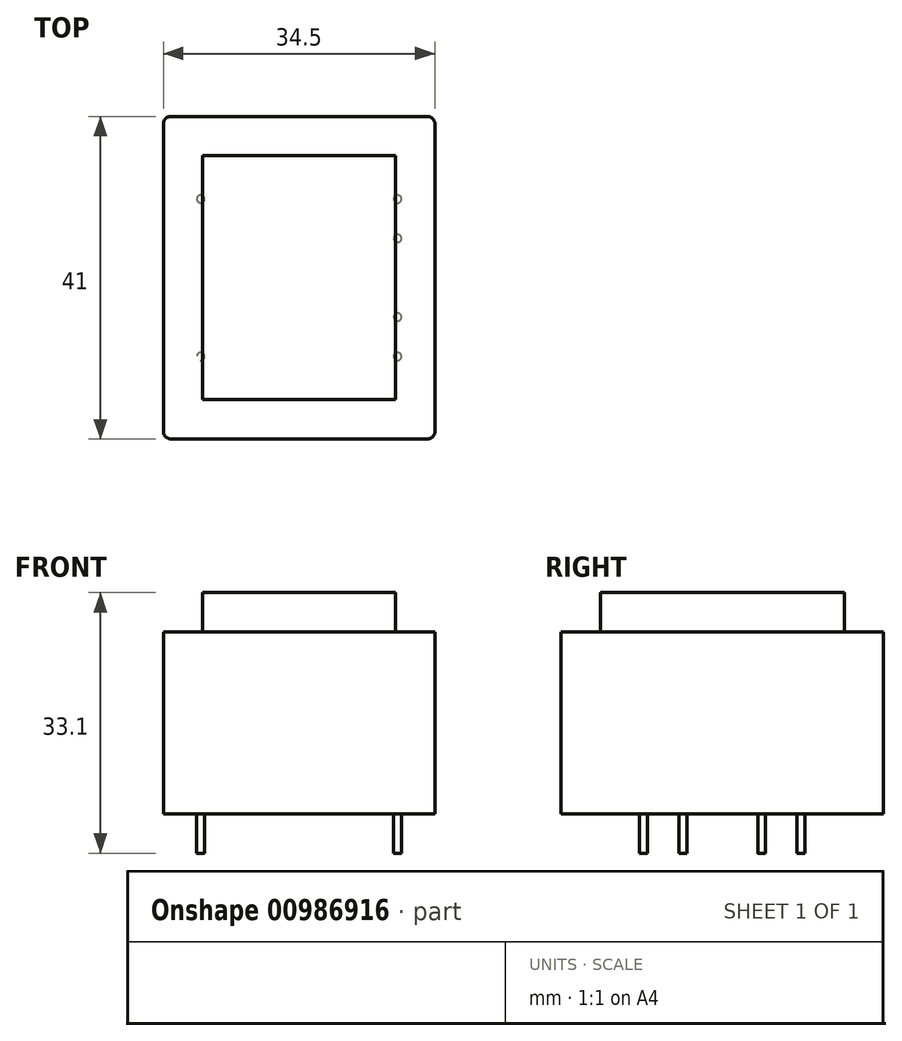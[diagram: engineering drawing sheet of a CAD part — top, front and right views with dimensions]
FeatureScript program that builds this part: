
annotation { "Feature Type Name" : "Feature", "Feature Type Description" : "" }
export const myFeature = defineFeature(function(context is Context, id is Id, definition is map)
    precondition{}
    {
        {
            var Q0;
            Q0=qCreatedBy(makeId("Top.planeOp"),FACE);
            var sketch = newSketch(context, id + "F0", { "sketchPlane" : qUnion([Q0])});
            skLineSegment(sketch, "E0.bottom", {"start": v(17.25, 20.5) * mm, "end": v(-17.25, 20.5) * mm});
            skLineSegment(sketch, "E0.top", {"start": v(17.25, -20.5) * mm, "end": v(-17.25, -20.5) * mm});
            skLineSegment(sketch, "E0.left", {"start": v(17.25, 20.5) * mm, "end": v(17.25, -20.5) * mm});
            skLineSegment(sketch, "E0.right", {"start": v(-17.25, 20.5) * mm, "end": v(-17.25, -20.5) * mm});
            skPoint(sketch, "E0.middle", {"position": v(0, 0) * mm});
            skSolve(sketch);
        }
        {
            var Q0;
            Q0=makeQuery(id+"F0.imprint","IMPRINT",FACE,{"disambiguationData":[TD([[makeQuery(id+"F0.imprint","IMPRINT",EDGE,{"derivedFrom":sQuery(id+"F0.wireOp",EDGE,"E0.bottom")}),1.0]])]});
            extrude(context, id + "F1", {"entities" : qUnion([Q0]), "depth" : 28.1 * mm, "offsetDistance" : 25 * mm});
        }
        {
            var Q0;
            Q0=makeQuery(id+"F1.opExtrude","CAP_FACE",FACE,{"disambiguationData":[OSD([sQuery(id+"F0.wireOp",EDGE,"E0.bottom"),sQuery(id+"F0.wireOp",EDGE,"E0.top"),sQuery(id+"F0.wireOp",EDGE,"E0.left"),sQuery(id+"F0.wireOp",EDGE,"E0.right")])],"isStart":true});
            var sketch = newSketch(context, id + "F2", { "sketchPlane" : qUnion([Q0])});
            skLineSegment(sketch, "E1.bottom", {"start": v(12.5, 10) * mm, "end": v(-12.5, 10) * mm, "construction": true});
            skLineSegment(sketch, "E1.top", {"start": v(12.5, -10) * mm, "end": v(-12.5, -10) * mm, "construction": true});
            skLineSegment(sketch, "E1.left", {"start": v(12.5, 10) * mm, "end": v(12.5, -10) * mm, "construction": true});
            skLineSegment(sketch, "E1.right", {"start": v(-12.5, 10) * mm, "end": v(-12.5, -10) * mm, "construction": true});
            skPoint(sketch, "E1.middle", {"position": v(0, 0) * mm});
            skCircle(sketch, "E2", {"center": v(-12.5, 10) * mm, "radius": 0.5 * mm});
            skCircle(sketch, "E3", {"center": v(-12.5, -10) * mm, "radius": 0.5 * mm});
            skCircle(sketch, "E4", {"center": v(12.5, 10) * mm, "radius": 0.5 * mm});
            skCircle(sketch, "E5", {"center": v(12.5, -10) * mm, "radius": 0.5 * mm});
            skCircle(sketch, "E6", {"center": v(12.5, -5) * mm, "radius": 0.5 * mm});
            skCircle(sketch, "E7", {"center": v(12.5, 5) * mm, "radius": 0.5 * mm});
            skSolve(sketch);
        }
        {
            var Q0;
            Q0 = qSketchRegion(id + "F2", true);
            extrude(context, id + "F3", {"entities" : qUnion([Q0]), "operationType" : NewBodyOperationType.ADD, "depth" : 5 * mm, "offsetDistance" : 25 * mm});
        }
        {
            var Q0;
            Q0=makeQuery(id+"F1.opExtrude","CAP_FACE",FACE,{"disambiguationData":[OSD([sQuery(id+"F0.wireOp",EDGE,"E0.bottom"),sQuery(id+"F0.wireOp",EDGE,"E0.top"),sQuery(id+"F0.wireOp",EDGE,"E0.left"),sQuery(id+"F0.wireOp",EDGE,"E0.right")])],"isStart":false});
            var sketch = newSketch(context, id + "F4", { "sketchPlane" : qUnion([Q0])});
            skLineSegment(sketch, "E8.0", {"start": v(12.25, 15.5) * mm, "end": v(-12.25, 15.5) * mm});
            skLineSegment(sketch, "E8.1", {"start": v(12.25, 15.5) * mm, "end": v(12.25, -15.5) * mm});
            skLineSegment(sketch, "E8.2", {"start": v(12.25, -15.5) * mm, "end": v(-12.25, -15.5) * mm});
            skLineSegment(sketch, "E8.3", {"start": v(-12.25, 15.5) * mm, "end": v(-12.25, -15.5) * mm});
            skSolve(sketch);
        }
        {
            var Q0;
            Q0=makeQuery(id+"F4.imprint","IMPRINT",FACE,{"disambiguationData":[TD([[makeQuery(id+"F4.imprint","IMPRINT",EDGE,{"derivedFrom":sQuery(id+"F4.wireOp",EDGE,"E8.0")}),-1.0]])]});
            extrude(context, id + "F5", {"entities" : qUnion([Q0]), "operationType" : NewBodyOperationType.REMOVE, "oppositeDirection" : true, "depth" : 5 * mm, "offsetDistance" : 25 * mm});
        }
        {
            var Q0;
            Q0=makeQuery(id+"F5.boolean.opBoolean","COPY",EDGE,{"derivedFrom":makeQuery(id+"F5.opExtrude","CAP_EDGE",EDGE,{"disambiguationData":[OSD([sQuery(id+"F4.wireOp",EDGE,"E8.3")])],"isStart":true})});
            var Q1;
            Q1=makeQuery(id+"F5.boolean.opBoolean","COPY",EDGE,{"derivedFrom":makeQuery(id+"F5.opExtrude","CAP_EDGE",EDGE,{"disambiguationData":[OSD([sQuery(id+"F4.wireOp",EDGE,"E8.2")])],"isStart":true})});
            var Q2;
            Q2=makeQuery(id+"F5.boolean.opBoolean","COPY",EDGE,{"derivedFrom":makeQuery(id+"F5.opExtrude","CAP_EDGE",EDGE,{"disambiguationData":[OSD([sQuery(id+"F4.wireOp",EDGE,"E8.1")])],"isStart":true})});
            var Q3;
            Q3=makeQuery(id+"F5.boolean.opBoolean","COPY",EDGE,{"derivedFrom":makeQuery(id+"F5.opExtrude","CAP_EDGE",EDGE,{"disambiguationData":[OSD([sQuery(id+"F4.wireOp",EDGE,"E8.0")])],"isStart":true})});
            var Q4;
            Q4=makeQuery(id+"F1.opExtrude","SWEPT_EDGE",EDGE,{"disambiguationData":[OSD([sQuery(id+"F0.wireOp",EDGE,"E0.top"),sQuery(id+"F0.wireOp",EDGE,"E0.left")])]});
            var Q5;
            Q5=makeQuery(id+"F1.opExtrude","SWEPT_EDGE",EDGE,{"disambiguationData":[OSD([sQuery(id+"F0.wireOp",EDGE,"E0.bottom"),sQuery(id+"F0.wireOp",EDGE,"E0.left")])]});
            var Q6;
            Q6=makeQuery(id+"F1.opExtrude","SWEPT_EDGE",EDGE,{"disambiguationData":[OSD([sQuery(id+"F0.wireOp",EDGE,"E0.top"),sQuery(id+"F0.wireOp",EDGE,"E0.right")])]});
            var Q7;
            Q7=makeQuery(id+"F5.boolean.opBoolean","COPY",EDGE,{"derivedFrom":makeQuery(id+"F5.opExtrude","CAP_EDGE",EDGE,{"disambiguationData":[OSD([sQuery(id+"F0.wireOp",EDGE,"E0.top")])],"isStart":false})});
            var Q8;
            Q8=makeQuery(id+"F5.boolean.opBoolean","COPY",EDGE,{"derivedFrom":makeQuery(id+"F5.opExtrude","CAP_EDGE",EDGE,{"disambiguationData":[OSD([sQuery(id+"F0.wireOp",EDGE,"E0.left")])],"isStart":false})});
            var Q9;
            Q9=makeQuery(id+"F5.boolean.opBoolean","COPY",EDGE,{"derivedFrom":makeQuery(id+"F5.opExtrude","CAP_EDGE",EDGE,{"disambiguationData":[OSD([sQuery(id+"F0.wireOp",EDGE,"E0.bottom")])],"isStart":false})});
            var Q10;
            Q10=makeQuery(id+"F5.boolean.opBoolean","COPY",EDGE,{"derivedFrom":makeQuery(id+"F5.opExtrude","CAP_EDGE",EDGE,{"disambiguationData":[OSD([sQuery(id+"F0.wireOp",EDGE,"E0.right")])],"isStart":false})});
            var Q11;
            Q11=makeQuery(id+"F1.opExtrude","SWEPT_EDGE",EDGE,{"disambiguationData":[OSD([sQuery(id+"F0.wireOp",EDGE,"E0.bottom"),sQuery(id+"F0.wireOp",EDGE,"E0.right")])]});
            fillet(context, id + "F6", {"entities" : qUnion([Q0, Q1, Q2, Q3, Q4, Q5, Q6, Q7, Q8, Q9, Q10, Q11]), "radius" : 1 * mm, "tangentPropagation" : true, "allowEdgeOverflow" : false});
        }
    });
